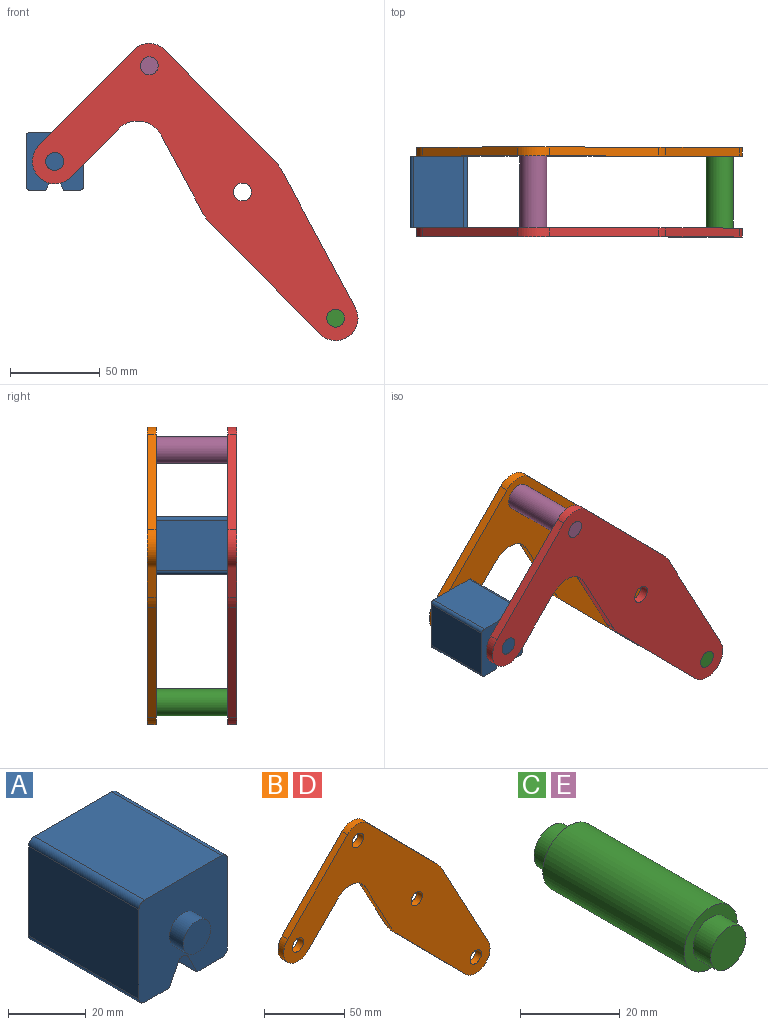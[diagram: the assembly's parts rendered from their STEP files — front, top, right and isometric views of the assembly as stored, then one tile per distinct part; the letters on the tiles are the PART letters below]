
ASSEMBLY  parts=5 mates=3
PART A: 18 faces, bbox 32.1x50x32.1 mm
  f0: plane 40x28.08mm, normal (1,0,0), area 1123.1mm2, adj f4,f10,f13,f14
  f1: plane 40x9.04mm, normal (0,0,-1), area 361.6mm2, adj f2,f4,f10,f14
  f2: plane 40x6.42mm, normal (-0.89,0,-0.45), area 287.2mm2, adj f1,f4,f10,f15
  f3: plane 40x6.42mm, normal (0.89,0,-0.45), area 287.2mm2, adj f4,f5,f10,f15
  f4: plane 32.08x32.08mm, normal (0,-1,0), area 900.6mm2, adj f0,f1,f2,f3,f5,f6,f7,f9
  f5: plane 40x9.04mm, normal (0,0,-1), area 361.6mm2, adj f3,f4,f10,f16
  f6: plane 40x28.08mm, normal (0,0,1), area 1123.1mm2, adj f4,f10,f13,f17
  f7: plane 40x28.08mm, normal (-1,0,0), area 1123.1mm2, adj f4,f10,f16,f17
  f8: plane 10x10mm, normal (0,-1,0), area 78.5mm2, adj f9
  f9: cylinder r=5mm len=10mm, axis (0,1,0), area 157.1mm2, adj f4,f8
  f10: plane 32.08x32.08mm, normal (0,1,0), area 900.6mm2, adj f0,f1,f2,f3,f5,f6,f7,f12
  f11: plane 10x10mm, normal (0,1,0), area 78.5mm2, adj f12
  f12: cylinder r=5mm len=10mm, axis (0,-1,0), area 157.1mm2, adj f10,f11
  f13: cylinder r=2mm len=40mm, axis (0,1,0), area 125.7mm2, adj f0,f4,f6,f10
  f14: cylinder r=2mm len=40mm, axis (0,-1,0), area 125.7mm2, adj f0,f1,f4,f10
  f15: cylinder r=2mm len=40mm, axis (0,1,0), area 177.1mm2, adj f2,f3,f4,f10
  f16: cylinder r=2mm len=40mm, axis (0,1,0), area 125.7mm2, adj f4,f5,f7,f10
  f17: cylinder r=2mm len=40mm, axis (0,-1,0), area 125.7mm2, adj f4,f6,f7,f10
PART B: 18 faces, bbox 181.7x5x165.8 mm
  f0: plane 43.49x23.35mm, normal (-0.88,0,-0.47), area 246.8mm2, adj f1,f14,f16,f17
  f1: cylinder r=25mm len=5.75mm, axis (0,1,0), area 35.8mm2, adj f0,f2,f16,f17
  f2: plane 61.6x60.87mm, normal (-0.71,0,-0.7), area 433mm2, adj f1,f3,f16,f17
  f3: cylinder r=12.5mm len=21.39mm, axis (0,1,0), area 178.4mm2, adj f2,f4,f16,f17
  f4: plane 76.3x40.96mm, normal (0.88,0,0.47), area 433mm2, adj f3,f5,f16,f17
  f5: cylinder r=25mm len=5.75mm, axis (0,1,0), area 35.8mm2, adj f4,f6,f16,f17
  f6: plane 61.6x60.87mm, normal (0.71,0,0.7), area 433mm2, adj f5,f7,f16,f17
  f7: cylinder r=12.5mm len=17.78mm, axis (0,1,0), area 98.9mm2, adj f6,f8,f16,f17
  f8: plane 53.35x52.71mm, normal (-0.71,0,0.7), area 375mm2, adj f7,f9,f16,f17
  f9: cylinder r=12.5mm len=21.39mm, axis (0,1,0), area 196.3mm2, adj f8,f10,f16,f17
  f10: plane 26.86x26.54mm, normal (0.71,0,-0.7), area 188.8mm2, adj f9,f14,f16,f17
  f11: cylinder r=5mm len=10mm, axis (0,1,0), area 157.1mm2, adj f16,f17
  f12: cylinder r=5mm len=10mm, axis (0,1,0), area 157.1mm2, adj f16,f17
  f13: cylinder r=5mm len=10mm, axis (0,1,0), area 157.1mm2, adj f16,f17
  f14: cylinder r=15mm len=23.89mm, axis (0,1,0), area 140.2mm2, adj f0,f10,f16,f17
  f15: cylinder r=5mm len=10mm, axis (0,1,0), area 157.1mm2, adj f16,f17
  f16: plane 181.66x165.78mm, normal (0,-1,0), area 8710.1mm2, adj f0,f1,f2,f3,f4,f5,f6,f7
  f17: plane 181.66x165.78mm, normal (0,1,0), area 8710.1mm2, adj f0,f1,f2,f3,f4,f5,f6,f7
PART C: 7 faces, bbox 15x50x15 mm
  f0: cylinder r=7.5mm len=40mm, axis (0,-1,0), area 1885mm2, adj f2,f5
  f1: cylinder r=5mm len=10mm, axis (0,1,0), area 157.1mm2, adj f2,f3
  f2: plane 15x15mm, normal (0,-1,0), area 98.2mm2, adj f0,f1
  f3: plane 10x10mm, normal (0,-1,0), area 78.5mm2, adj f1
  f4: cylinder r=5mm len=10mm, axis (0,-1,0), area 157.1mm2, adj f5,f6
  f5: plane 15x15mm, normal (0,1,0), area 98.2mm2, adj f0,f4
  f6: plane 10x10mm, normal (0,1,0), area 78.5mm2, adj f4
PART D: same geometry as B
PART E: same geometry as C
PLACE A at identity
PLACE B t=(0,45,0)mm
PLACE C t=(103.95,0,-140.78)mm
PLACE D at identity fixed
PLACE E at identity
MATE fastened C.f0 <-> D.f3  axis (0,-1,0) through (51.98,0,-70.39)mm
MATE fastened B.f7 <-> E.f0  axis (0,-1,0) through (-51.98,40,70.39)mm
MATE revolute A.f9 <-> D.f9  axis (0,-1,0) through (-104.69,0,17.04)mm
